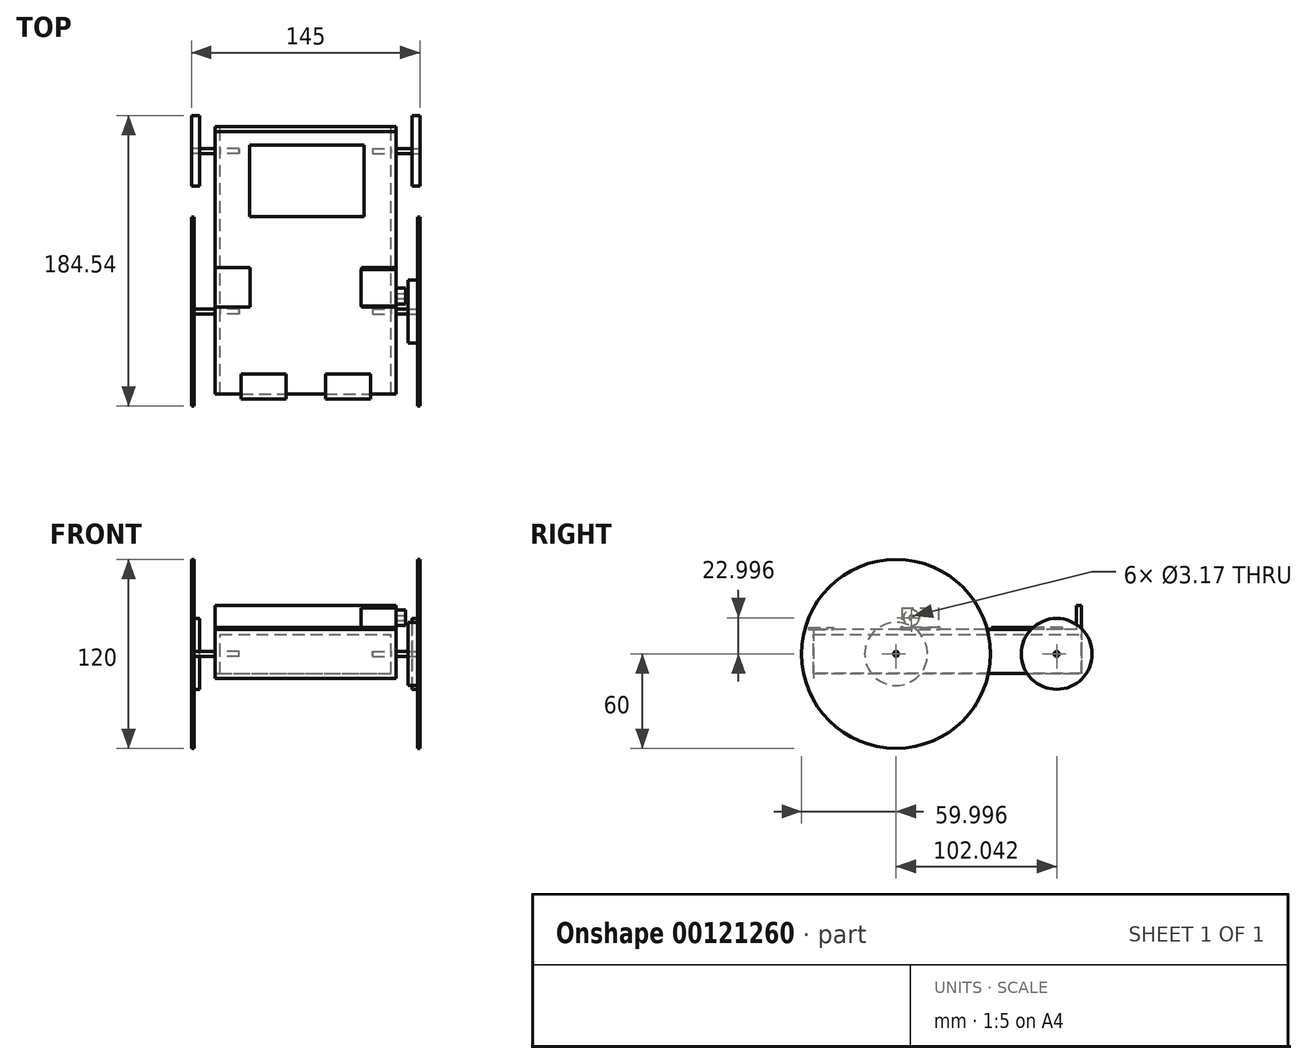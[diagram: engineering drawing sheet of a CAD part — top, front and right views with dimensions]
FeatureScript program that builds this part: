
annotation { "Feature Type Name" : "Feature", "Feature Type Description" : "" }
export const myFeature = defineFeature(function(context is Context, id is Id, definition is map)
    precondition{}
    {
        {
            var Q0;
            Q0=qCreatedBy(makeId("Top.planeOp"),FACE);
            var sketch = newSketch(context, id + "F0", { "sketchPlane" : qUnion([Q0])});
            skLineSegment(sketch, "E0.bottom", {"start": v(-104.64, 92.67) * mm, "end": v(10.36, 92.67) * mm});
            skLineSegment(sketch, "E0.top", {"start": v(-104.64, -77.33) * mm, "end": v(10.36, -77.33) * mm});
            skLineSegment(sketch, "E0.left", {"start": v(-104.64, 92.67) * mm, "end": v(-104.64, -77.33) * mm});
            skLineSegment(sketch, "E0.right", {"start": v(10.36, 92.67) * mm, "end": v(10.36, -77.33) * mm});
            skSolve(sketch);
        }
        {
            var Q0;
            Q0 = qSketchRegion(id + "F0", true);
            extrude(context, id + "F1", {"entities" : qUnion([Q0]), "depth" : 3.17 * mm});
        }
        {
            var Q0;
            Q0=makeQuery(id+"F1.opExtrude","CAP_FACE",FACE,{"disambiguationData":[OSD([sQuery(id+"F0.wireOp",EDGE,"E0.bottom"),sQuery(id+"F0.wireOp",EDGE,"E0.top"),sQuery(id+"F0.wireOp",EDGE,"E0.left"),sQuery(id+"F0.wireOp",EDGE,"E0.right")])],"isStart":true});
            var sketch = newSketch(context, id + "F2", { "sketchPlane" : qUnion([Q0])});
            skLineSegment(sketch, "E1.bottom", {"start": v(-104.64, 77.33) * mm, "end": v(-101.47, 77.33) * mm});
            skLineSegment(sketch, "E1.top", {"start": v(-104.64, -92.67) * mm, "end": v(-101.47, -92.67) * mm});
            skLineSegment(sketch, "E1.left", {"start": v(-104.64, 77.33) * mm, "end": v(-104.64, -92.67) * mm});
            skLineSegment(sketch, "E1.right", {"start": v(-101.47, 77.33) * mm, "end": v(-101.47, -92.67) * mm});
            skLineSegment(sketch, "E2.bottom", {"start": v(10.36, 77.33) * mm, "end": v(7.18, 77.33) * mm});
            skLineSegment(sketch, "E2.top", {"start": v(10.36, -92.67) * mm, "end": v(7.18, -92.67) * mm});
            skLineSegment(sketch, "E2.left", {"start": v(10.36, 77.33) * mm, "end": v(10.36, -92.67) * mm});
            skLineSegment(sketch, "E2.right", {"start": v(7.18, 77.33) * mm, "end": v(7.18, -92.67) * mm});
            skLineSegment(sketch, "E3.bottom", {"start": v(-68.47, 77.33) * mm, "end": v(-65.3, 77.33) * mm});
            skLineSegment(sketch, "E3.top", {"start": v(-68.47, -92.67) * mm, "end": v(-65.3, -92.67) * mm});
            skLineSegment(sketch, "E4.bottom", {"start": v(-29, 77.33) * mm, "end": v(-25.82, 77.33) * mm});
            skLineSegment(sketch, "E4.top", {"start": v(-29, -92.67) * mm, "end": v(-25.82, -92.67) * mm});
            skSolve(sketch);
        }
        {
            var Q0;
            Q0 = qSketchRegion(id + "F2", true);
            extrude(context, id + "F3", {"entities" : qUnion([Q0]), "operationType" : NewBodyOperationType.ADD, "depth" : 25 * mm});
        }
        {
            var Q0;
            Q0=makeQuery(id+"F3.opExtrude","CAP_FACE",FACE,{"disambiguationData":[OSD([sQuery(id+"F2.wireOp",EDGE,"E1.bottom"),sQuery(id+"F2.wireOp",EDGE,"E1.top"),sQuery(id+"F2.wireOp",EDGE,"E1.left"),sQuery(id+"F2.wireOp",EDGE,"E1.right")])],"isStart":false});
            var sketch = newSketch(context, id + "F4", { "sketchPlane" : qUnion([Q0])});
            skLineSegment(sketch, "E5.bottom", {"start": v(-104.64, 77.33) * mm, "end": v(10.36, 77.33) * mm});
            skLineSegment(sketch, "E5.top", {"start": v(-104.64, -92.67) * mm, "end": v(10.36, -92.67) * mm});
            skLineSegment(sketch, "E5.left", {"start": v(-104.64, 77.33) * mm, "end": v(-104.64, -92.67) * mm});
            skLineSegment(sketch, "E5.right", {"start": v(10.36, 77.33) * mm, "end": v(10.36, -92.67) * mm});
            skSolve(sketch);
        }
        {
            var Q0;
            Q0 = qSketchRegion(id + "F4", true);
            extrude(context, id + "F5", {"entities" : qUnion([Q0]), "operationType" : NewBodyOperationType.ADD, "depth" : 1 / 203.2 * mm});
        }
        {
            var Q0;
            Q0=makeQuery(id+"F5.boolean.opBoolean","MERGE",FACE,{"derivedFrom":[makeQuery(id+"F3.boolean.opBoolean","MERGE",FACE,{"derivedFrom":[makeQuery(id+"F1.opExtrude","SWEPT_FACE",FACE,{"disambiguationData":[OSD([sQuery(id+"F0.wireOp",EDGE,"E0.top")])]}),makeQuery(id+"F3.opExtrude","SWEPT_FACE",FACE,{"disambiguationData":[OSD([sQuery(id+"F2.wireOp",EDGE,"E1.bottom")])]}),makeQuery(id+"F3.opExtrude","SWEPT_FACE",FACE,{"disambiguationData":[OSD([sQuery(id+"F2.wireOp",EDGE,"E2.bottom")])]})]}),makeQuery(id+"F5.opExtrude","SWEPT_FACE",FACE,{"disambiguationData":[OSD([sQuery(id+"F4.wireOp",EDGE,"E5.bottom")])]})]});
            var sketch = newSketch(context, id + "F6", { "sketchPlane" : qUnion([Q0])});
            skLineSegment(sketch, "E6.bottom", {"start": v(-104.64, 3.18) * mm, "end": v(10.36, 3.18) * mm});
            skLineSegment(sketch, "E6.top", {"start": v(-104.64, -28.18) * mm, "end": v(10.36, -28.18) * mm});
            skLineSegment(sketch, "E6.left", {"start": v(-104.64, 3.18) * mm, "end": v(-104.64, -28.18) * mm});
            skLineSegment(sketch, "E6.right", {"start": v(10.36, 3.18) * mm, "end": v(10.36, -28.18) * mm});
            skSolve(sketch);
        }
        {
            var Q0;
            Q0 = qSketchRegion(id + "F6", true);
            extrude(context, id + "F7", {"entities" : qUnion([Q0]), "operationType" : NewBodyOperationType.ADD, "depth" : 1 / 203.2 * mm});
        }
        {
            var Q0;
            Q0=makeQuery(id+"F7.boolean.opBoolean","MERGE",FACE,{"derivedFrom":[makeQuery(id+"F1.opExtrude","CAP_FACE",FACE,{"disambiguationData":[OSD([sQuery(id+"F0.wireOp",EDGE,"E0.bottom"),sQuery(id+"F0.wireOp",EDGE,"E0.top"),sQuery(id+"F0.wireOp",EDGE,"E0.left"),sQuery(id+"F0.wireOp",EDGE,"E0.right")])],"isStart":false}),makeQuery(id+"F7.opExtrude","SWEPT_FACE",FACE,{"disambiguationData":[OSD([sQuery(id+"F6.wireOp",EDGE,"E6.bottom")])]})]});
            var sketch = newSketch(context, id + "F8", { "sketchPlane" : qUnion([Q0])});
            skLineSegment(sketch, "E7.bottom", {"start": v(-104.64, 92.67) * mm, "end": v(10.36, 92.67) * mm});
            skLineSegment(sketch, "E7.top", {"start": v(-104.64, 89.5) * mm, "end": v(10.36, 89.5) * mm});
            skLineSegment(sketch, "E7.left", {"start": v(-104.64, 92.67) * mm, "end": v(-104.64, 89.5) * mm});
            skLineSegment(sketch, "E7.right", {"start": v(10.36, 92.67) * mm, "end": v(10.36, 89.5) * mm});
            skSolve(sketch);
        }
        {
            var Q0;
            Q0 = qSketchRegion(id + "F8", true);
            extrude(context, id + "F9", {"entities" : qUnion([Q0]), "operationType" : NewBodyOperationType.ADD, "depth" : 15 * mm});
        }
        {
            var Q0;
            Q0=makeQuery(id+"F9.boolean.opBoolean","MERGE",FACE,{"derivedFrom":[makeQuery(id+"F7.boolean.opBoolean","MERGE",FACE,{"derivedFrom":[makeQuery(id+"F5.boolean.opBoolean","MERGE",FACE,{"derivedFrom":[makeQuery(id+"F3.boolean.opBoolean","MERGE",FACE,{"derivedFrom":[makeQuery(id+"F1.opExtrude","SWEPT_FACE",FACE,{"disambiguationData":[OSD([sQuery(id+"F0.wireOp",EDGE,"E0.right")])]}),makeQuery(id+"F3.opExtrude","SWEPT_FACE",FACE,{"disambiguationData":[OSD([sQuery(id+"F2.wireOp",EDGE,"E2.left")])]})]}),makeQuery(id+"F5.opExtrude","SWEPT_FACE",FACE,{"disambiguationData":[OSD([sQuery(id+"F4.wireOp",EDGE,"E5.right")])]})]}),makeQuery(id+"F7.opExtrude","SWEPT_FACE",FACE,{"disambiguationData":[OSD([sQuery(id+"F6.wireOp",EDGE,"E6.right")])]})]}),makeQuery(id+"F9.opExtrude","SWEPT_FACE",FACE,{"disambiguationData":[OSD([sQuery(id+"F8.wireOp",EDGE,"E7.right")])]})]});
            var sketch = newSketch(context, id + "F10", { "sketchPlane" : qUnion([Q0])});
            skCircle(sketch, "E8", {"center": v(-24.94, -12.5) * mm, "radius": 1.59 * mm});
            skPoint(sketch, "E8.centerSnap0", {"position": v(-80.5, -12.5) * mm});
            skCircle(sketch, "E9", {"center": v(77.1, -12.5) * mm, "radius": 1.59 * mm});
            skSolve(sketch);
        }
        {
            var Q0;
            Q0 = qSketchRegion(id + "F10", true);
            extrude(context, id + "F11", {"entities" : qUnion([Q0]), "operationType" : NewBodyOperationType.REMOVE, "endBound" : BoundingType.THROUGH_ALL, "oppositeDirection" : true, "depth" : 25 * mm});
        }
        {
            var Q0;
            Q0=makeQuery(id+"F9.boolean.opBoolean","MERGE",FACE,{"derivedFrom":[makeQuery(id+"F7.boolean.opBoolean","MERGE",FACE,{"derivedFrom":[makeQuery(id+"F5.boolean.opBoolean","MERGE",FACE,{"derivedFrom":[makeQuery(id+"F3.boolean.opBoolean","MERGE",FACE,{"derivedFrom":[makeQuery(id+"F1.opExtrude","SWEPT_FACE",FACE,{"disambiguationData":[OSD([sQuery(id+"F0.wireOp",EDGE,"E0.right")])]}),makeQuery(id+"F3.opExtrude","SWEPT_FACE",FACE,{"disambiguationData":[OSD([sQuery(id+"F2.wireOp",EDGE,"E2.left")])]})]}),makeQuery(id+"F5.opExtrude","SWEPT_FACE",FACE,{"disambiguationData":[OSD([sQuery(id+"F4.wireOp",EDGE,"E5.right")])]})]}),makeQuery(id+"F7.opExtrude","SWEPT_FACE",FACE,{"disambiguationData":[OSD([sQuery(id+"F6.wireOp",EDGE,"E6.right")])]})]}),makeQuery(id+"F9.opExtrude","SWEPT_FACE",FACE,{"disambiguationData":[OSD([sQuery(id+"F8.wireOp",EDGE,"E7.right")])]})]});
            var sketch = newSketch(context, id + "F12", { "sketchPlane" : qUnion([Q0])});
            skCircle(sketch, "E10", {"center": v(-24.94, -12.5) * mm, "radius": 1.59 * mm});
            skSolve(sketch);
        }
        {
            var Q0;
            Q0 = qSketchRegion(id + "F12", true);
            extrude(context, id + "F13", {"entities" : qUnion([Q0]), "oppositeDirection" : true, "depth" : 15 * mm});
        }
        {
            var Q0;
            Q0=makeQuery(id+"F13.opExtrude","CAP_FACE",FACE,{"disambiguationData":[OSD([sQuery(id+"F12.wireOp",EDGE,"E10")])],"isStart":true});
            var sketch = newSketch(context, id + "F14", { "sketchPlane" : qUnion([Q0])});
            skCircle(sketch, "E11", {"center": v(-24.94, -12.5) * mm, "radius": 1.59 * mm});
            skSolve(sketch);
        }
        {
            var Q0;
            Q0 = qSketchRegion(id + "F14", true);
            extrude(context, id + "F15", {"entities" : qUnion([Q0]), "operationType" : NewBodyOperationType.ADD, "depth" : 15 * mm});
        }
        {
            var Q0;
            Q0=makeQuery(id+"F9.boolean.opBoolean","MERGE",FACE,{"derivedFrom":[makeQuery(id+"F7.boolean.opBoolean","MERGE",FACE,{"derivedFrom":[makeQuery(id+"F5.boolean.opBoolean","MERGE",FACE,{"derivedFrom":[makeQuery(id+"F3.boolean.opBoolean","MERGE",FACE,{"derivedFrom":[makeQuery(id+"F1.opExtrude","SWEPT_FACE",FACE,{"disambiguationData":[OSD([sQuery(id+"F0.wireOp",EDGE,"E0.right")])]}),makeQuery(id+"F3.opExtrude","SWEPT_FACE",FACE,{"disambiguationData":[OSD([sQuery(id+"F2.wireOp",EDGE,"E2.left")])]})]}),makeQuery(id+"F5.opExtrude","SWEPT_FACE",FACE,{"disambiguationData":[OSD([sQuery(id+"F4.wireOp",EDGE,"E5.right")])]})]}),makeQuery(id+"F7.opExtrude","SWEPT_FACE",FACE,{"disambiguationData":[OSD([sQuery(id+"F6.wireOp",EDGE,"E6.right")])]})]}),makeQuery(id+"F9.opExtrude","SWEPT_FACE",FACE,{"disambiguationData":[OSD([sQuery(id+"F8.wireOp",EDGE,"E7.right")])]})]});
            var sketch = newSketch(context, id + "F16", { "sketchPlane" : qUnion([Q0])});
            skCircle(sketch, "E12", {"center": v(77.1, -12.5) * mm, "radius": 1.59 * mm});
            skSolve(sketch);
        }
        {
            var Q0;
            Q0 = qSketchRegion(id + "F16", true);
            extrude(context, id + "F17", {"entities" : qUnion([Q0]), "oppositeDirection" : true, "depth" : 15 * mm});
        }
        {
            var Q0;
            Q0=makeQuery(id+"F17.opExtrude","CAP_FACE",FACE,{"disambiguationData":[OSD([sQuery(id+"F16.wireOp",EDGE,"E12")])],"isStart":true});
            var sketch = newSketch(context, id + "F18", { "sketchPlane" : qUnion([Q0])});
            skCircle(sketch, "E13", {"center": v(77.1, -12.5) * mm, "radius": 1.59 * mm});
            skSolve(sketch);
        }
        {
            var Q0;
            Q0 = qSketchRegion(id + "F18", true);
            extrude(context, id + "F19", {"entities" : qUnion([Q0]), "operationType" : NewBodyOperationType.ADD, "depth" : 15 * mm});
        }
        {
            var Q0;
            Q0=makeQuery(id+"F9.boolean.opBoolean","MERGE",FACE,{"derivedFrom":[makeQuery(id+"F7.boolean.opBoolean","MERGE",FACE,{"derivedFrom":[makeQuery(id+"F5.boolean.opBoolean","MERGE",FACE,{"derivedFrom":[makeQuery(id+"F3.boolean.opBoolean","MERGE",FACE,{"derivedFrom":[makeQuery(id+"F1.opExtrude","SWEPT_FACE",FACE,{"disambiguationData":[OSD([sQuery(id+"F0.wireOp",EDGE,"E0.left")])]}),makeQuery(id+"F3.opExtrude","SWEPT_FACE",FACE,{"disambiguationData":[OSD([sQuery(id+"F2.wireOp",EDGE,"E1.left")])]})]}),makeQuery(id+"F5.opExtrude","SWEPT_FACE",FACE,{"disambiguationData":[OSD([sQuery(id+"F4.wireOp",EDGE,"E5.left")])]})]}),makeQuery(id+"F7.opExtrude","SWEPT_FACE",FACE,{"disambiguationData":[OSD([sQuery(id+"F6.wireOp",EDGE,"E6.left")])]})]}),makeQuery(id+"F9.opExtrude","SWEPT_FACE",FACE,{"disambiguationData":[OSD([sQuery(id+"F8.wireOp",EDGE,"E7.left")])]})]});
            var sketch = newSketch(context, id + "F20", { "sketchPlane" : qUnion([Q0])});
            skCircle(sketch, "E14", {"center": v(24.94, -12.5) * mm, "radius": 1.59 * mm});
            skSolve(sketch);
        }
        {
            var Q0;
            Q0 = qSketchRegion(id + "F20", true);
            extrude(context, id + "F21", {"entities" : qUnion([Q0]), "oppositeDirection" : true, "depth" : 15 * mm});
        }
        {
            var Q0;
            Q0=makeQuery(id+"F21.opExtrude","CAP_FACE",FACE,{"disambiguationData":[OSD([sQuery(id+"F20.wireOp",EDGE,"E14")])],"isStart":true});
            var sketch = newSketch(context, id + "F22", { "sketchPlane" : qUnion([Q0])});
            skCircle(sketch, "E15", {"center": v(24.94, -12.5) * mm, "radius": 1.59 * mm});
            skSolve(sketch);
        }
        {
            var Q0;
            Q0 = qSketchRegion(id + "F22", true);
            extrude(context, id + "F23", {"entities" : qUnion([Q0]), "operationType" : NewBodyOperationType.ADD, "depth" : 15 * mm});
        }
        {
            var Q0;
            Q0=makeQuery(id+"F9.boolean.opBoolean","MERGE",FACE,{"derivedFrom":[makeQuery(id+"F7.boolean.opBoolean","MERGE",FACE,{"derivedFrom":[makeQuery(id+"F5.boolean.opBoolean","MERGE",FACE,{"derivedFrom":[makeQuery(id+"F3.boolean.opBoolean","MERGE",FACE,{"derivedFrom":[makeQuery(id+"F1.opExtrude","SWEPT_FACE",FACE,{"disambiguationData":[OSD([sQuery(id+"F0.wireOp",EDGE,"E0.left")])]}),makeQuery(id+"F3.opExtrude","SWEPT_FACE",FACE,{"disambiguationData":[OSD([sQuery(id+"F2.wireOp",EDGE,"E1.left")])]})]}),makeQuery(id+"F5.opExtrude","SWEPT_FACE",FACE,{"disambiguationData":[OSD([sQuery(id+"F4.wireOp",EDGE,"E5.left")])]})]}),makeQuery(id+"F7.opExtrude","SWEPT_FACE",FACE,{"disambiguationData":[OSD([sQuery(id+"F6.wireOp",EDGE,"E6.left")])]})]}),makeQuery(id+"F9.opExtrude","SWEPT_FACE",FACE,{"disambiguationData":[OSD([sQuery(id+"F8.wireOp",EDGE,"E7.left")])]})]});
            var sketch = newSketch(context, id + "F24", { "sketchPlane" : qUnion([Q0])});
            skCircle(sketch, "E16", {"center": v(-77.1, -12.5) * mm, "radius": 1.59 * mm});
            skSolve(sketch);
        }
        {
            var Q0;
            Q0 = qSketchRegion(id + "F24", true);
            extrude(context, id + "F25", {"entities" : qUnion([Q0]), "oppositeDirection" : true, "depth" : 15 * mm});
        }
        {
            var Q0;
            Q0=makeQuery(id+"F25.opExtrude","CAP_FACE",FACE,{"disambiguationData":[OSD([sQuery(id+"F24.wireOp",EDGE,"E16")])],"isStart":true});
            var sketch = newSketch(context, id + "F26", { "sketchPlane" : qUnion([Q0])});
            skCircle(sketch, "E17", {"center": v(-77.1, -12.5) * mm, "radius": 1.59 * mm});
            skSolve(sketch);
        }
        {
            var Q0;
            Q0 = qSketchRegion(id + "F26", true);
            extrude(context, id + "F27", {"entities" : qUnion([Q0]), "operationType" : NewBodyOperationType.ADD, "depth" : 15 * mm});
        }
        {
            var Q0;
            Q0=makeQuery(id+"F23.opExtrude","CAP_FACE",FACE,{"disambiguationData":[OSD([sQuery(id+"F22.wireOp",EDGE,"E15")])],"isStart":false});
            var sketch = newSketch(context, id + "F28", { "sketchPlane" : qUnion([Q0])});
            skCircle(sketch, "E18", {"center": v(24.94, -12.5) * mm, "radius": 60 * mm});
            skCircle(sketch, "E19", {"center": v(24.94, -12.5) * mm, "radius": 1.59 * mm});
            skSolve(sketch);
        }
        {
            var Q0;
            Q0=makeQuery(id+"F28.imprint","IMPRINT",FACE,{"disambiguationData":[TD([[makeQuery(id+"F28.imprint","IMPRINT",EDGE,{"derivedFrom":sQuery(id+"F28.wireOp",EDGE,"E18")}),1.0]])]});
            extrude(context, id + "F29", {"entities" : qUnion([Q0]), "oppositeDirection" : true, "depth" : 1.5 * mm});
        }
        {
            var Q0;
            Q0=makeQuery(id+"F15.opExtrude","CAP_FACE",FACE,{"disambiguationData":[OSD([sQuery(id+"F14.wireOp",EDGE,"E11")])],"isStart":false});
            var sketch = newSketch(context, id + "F30", { "sketchPlane" : qUnion([Q0])});
            skCircle(sketch, "E20", {"center": v(-24.94, -12.5) * mm, "radius": 60 * mm});
            skCircle(sketch, "E21", {"center": v(-24.94, -12.5) * mm, "radius": 1.59 * mm});
            skSolve(sketch);
        }
        {
            var Q0;
            Q0 = qSketchRegion(id + "F30", true);
            extrude(context, id + "F31", {"entities" : qUnion([Q0]), "oppositeDirection" : true, "depth" : 1.5 * mm});
        }
        {
            var Q0;
            Q0=makeQuery(id+"F19.opExtrude","CAP_FACE",FACE,{"disambiguationData":[OSD([sQuery(id+"F18.wireOp",EDGE,"E13")])],"isStart":false});
            var sketch = newSketch(context, id + "F32", { "sketchPlane" : qUnion([Q0])});
            skCircle(sketch, "E22", {"center": v(77.1, -12.5) * mm, "radius": 22.5 * mm});
            skSolve(sketch);
        }
        {
            var Q0;
            Q0=makeQuery(id+"F32.imprint","IMPRINT",FACE,{"disambiguationData":[TD([[makeQuery(id+"F32.imprint","IMPRINT",EDGE,{"derivedFrom":sQuery(id+"F32.wireOp",EDGE,"E22")}),1.0]])]});
            extrude(context, id + "F33", {"entities" : qUnion([Q0]), "oppositeDirection" : true, "depth" : 5 * mm});
        }
        {
            var Q0;
            Q0=makeQuery(id+"F27.opExtrude","CAP_FACE",FACE,{"disambiguationData":[OSD([sQuery(id+"F26.wireOp",EDGE,"E17")])],"isStart":false});
            var sketch = newSketch(context, id + "F34", { "sketchPlane" : qUnion([Q0])});
            skCircle(sketch, "E23", {"center": v(-77.1, -12.5) * mm, "radius": 22.5 * mm});
            skCircle(sketch, "E24", {"center": v(-77.1, -12.5) * mm, "radius": 1.59 * mm});
            skSolve(sketch);
        }
        {
            var Q0;
            Q0 = qSketchRegion(id + "F34", true);
            extrude(context, id + "F35", {"entities" : qUnion([Q0]), "oppositeDirection" : true, "depth" : 5 * mm});
        }
        {
            var Q0;
            Q0=makeQuery(id+"F31.opExtrude","CAP_FACE",FACE,{"disambiguationData":[OSD([sQuery(id+"F30.wireOp",EDGE,"E20"),sQuery(id+"F30.wireOp",EDGE,"E21")])],"isStart":false});
            var sketch = newSketch(context, id + "F36", { "sketchPlane" : qUnion([Q0])});
            skCircle(sketch, "E25", {"center": v(24.94, -12.5) * mm, "radius": 20 * mm});
            skCircle(sketch, "E26", {"center": v(24.94, -12.5) * mm, "radius": 1.59 * mm});
            skSolve(sketch);
        }
        {
            var Q0;
            Q0 = qSketchRegion(id + "F36", true);
            extrude(context, id + "F37", {"entities" : qUnion([Q0]), "depth" : 6 * mm});
        }
        {
            var Q0;
            Q0=makeQuery(id+"F7.boolean.opBoolean","MERGE",FACE,{"derivedFrom":[makeQuery(id+"F1.opExtrude","CAP_FACE",FACE,{"disambiguationData":[OSD([sQuery(id+"F0.wireOp",EDGE,"E0.bottom"),sQuery(id+"F0.wireOp",EDGE,"E0.top"),sQuery(id+"F0.wireOp",EDGE,"E0.left"),sQuery(id+"F0.wireOp",EDGE,"E0.right")])],"isStart":false}),makeQuery(id+"F7.opExtrude","SWEPT_FACE",FACE,{"disambiguationData":[OSD([sQuery(id+"F6.wireOp",EDGE,"E6.bottom")])]})]});
            var sketch = newSketch(context, id + "F38", { "sketchPlane" : qUnion([Q0])});
            skLineSegment(sketch, "E27.bottom", {"start": v(10.36, -22.18) * mm, "end": v(-11.64, -22.18) * mm});
            skLineSegment(sketch, "E27.top", {"start": v(10.36, 2.82) * mm, "end": v(-11.64, 2.82) * mm});
            skLineSegment(sketch, "E27.left", {"start": v(10.36, -22.18) * mm, "end": v(10.36, 2.82) * mm});
            skLineSegment(sketch, "E27.right", {"start": v(-11.64, -22.18) * mm, "end": v(-11.64, 2.82) * mm});
            skLineSegment(sketch, "E28.bottom", {"start": v(-82.64, -22.18) * mm, "end": v(-104.64, -22.18) * mm});
            skLineSegment(sketch, "E28.top", {"start": v(-82.64, 2.82) * mm, "end": v(-104.64, 2.82) * mm});
            skLineSegment(sketch, "E28.left", {"start": v(-82.64, -22.18) * mm, "end": v(-82.64, 2.82) * mm});
            skLineSegment(sketch, "E28.right", {"start": v(-104.64, -22.18) * mm, "end": v(-104.64, 2.82) * mm});
            skSolve(sketch);
        }
        {
            var Q0;
            Q0 = qSketchRegion(id + "F38", true);
            extrude(context, id + "F39", {"entities" : qUnion([Q0]), "operationType" : NewBodyOperationType.ADD, "depth" : 1 * mm});
        }
        {
            var Q0;
            Q0=makeQuery(id+"F39.opExtrude","CAP_FACE",FACE,{"disambiguationData":[OSD([sQuery(id+"F38.wireOp",EDGE,"E27.bottom"),sQuery(id+"F38.wireOp",EDGE,"E27.top"),sQuery(id+"F38.wireOp",EDGE,"E27.left"),sQuery(id+"F38.wireOp",EDGE,"E27.right")])],"isStart":false});
            var sketch = newSketch(context, id + "F40", { "sketchPlane" : qUnion([Q0])});
            skLineSegment(sketch, "E29.bottom", {"start": v(-11.88, -21.35) * mm, "end": v(10.12, -21.35) * mm});
            skLineSegment(sketch, "E29.top", {"start": v(-11.88, 1.85) * mm, "end": v(10.12, 1.85) * mm});
            skLineSegment(sketch, "E29.left", {"start": v(-11.88, -21.35) * mm, "end": v(-11.88, 1.85) * mm});
            skLineSegment(sketch, "E29.right", {"start": v(10.12, -21.35) * mm, "end": v(10.12, 1.85) * mm});
            skSolve(sketch);
        }
        {
            var Q0;
            Q0 = qSketchRegion(id + "F40", true);
            extrude(context, id + "F41", {"entities" : qUnion([Q0]), "depth" : 12.5 * mm});
        }
        {
            var Q0;
            Q0=makeQuery(id+"F41.opExtrude","SWEPT_FACE",FACE,{"disambiguationData":[OSD([sQuery(id+"F40.wireOp",EDGE,"E29.right")])]});
            var sketch = newSketch(context, id + "F42", { "sketchPlane" : qUnion([Q0])});
            skCircle(sketch, "E30", {"center": v(-15.2, 10.5) * mm, "radius": 1.59 * mm});
            skSolve(sketch);
        }
        {
            var Q0;
            Q0 = qSketchRegion(id + "F42", true);
            extrude(context, id + "F43", {"entities" : qUnion([Q0]), "operationType" : NewBodyOperationType.ADD, "depth" : 6 * mm});
        }
        {
            var Q0;
            Q0=makeQuery(id+"F43.opExtrude","CAP_FACE",FACE,{"disambiguationData":[OSD([sQuery(id+"F42.wireOp",EDGE,"E30")])],"isStart":false});
            var sketch = newSketch(context, id + "F44", { "sketchPlane" : qUnion([Q0])});
            skCircle(sketch, "E31", {"center": v(-15.2, 10.5) * mm, "radius": 5 * mm});
            skCircle(sketch, "E32", {"center": v(-15.2, 10.5) * mm, "radius": 1.59 * mm});
            skSolve(sketch);
        }
        {
            var Q0;
            Q0 = qSketchRegion(id + "F44", true);
            extrude(context, id + "F45", {"entities" : qUnion([Q0]), "oppositeDirection" : true, "depth" : 6 * mm});
        }
        {
            var Q0;
            Q0=makeQuery(id+"F7.boolean.opBoolean","MERGE",FACE,{"derivedFrom":[makeQuery(id+"F1.opExtrude","CAP_FACE",FACE,{"disambiguationData":[OSD([sQuery(id+"F0.wireOp",EDGE,"E0.bottom"),sQuery(id+"F0.wireOp",EDGE,"E0.top"),sQuery(id+"F0.wireOp",EDGE,"E0.left"),sQuery(id+"F0.wireOp",EDGE,"E0.right")])],"isStart":false}),makeQuery(id+"F7.opExtrude","SWEPT_FACE",FACE,{"disambiguationData":[OSD([sQuery(id+"F6.wireOp",EDGE,"E6.bottom")])]})]});
            var sketch = newSketch(context, id + "F46", { "sketchPlane" : qUnion([Q0])});
            skLineSegment(sketch, "E33.bottom", {"start": v(-82.74, 80.69) * mm, "end": v(-10, 80.69) * mm});
            skLineSegment(sketch, "E33.top", {"start": v(-82.74, 35.5) * mm, "end": v(-10, 35.5) * mm});
            skLineSegment(sketch, "E33.left", {"start": v(-82.74, 80.69) * mm, "end": v(-82.74, 35.5) * mm});
            skLineSegment(sketch, "E33.right", {"start": v(-10, 80.69) * mm, "end": v(-10, 35.5) * mm});
            skSolve(sketch);
        }
        {
            var Q0;
            Q0 = qSketchRegion(id + "F46", true);
            extrude(context, id + "F47", {"entities" : qUnion([Q0]), "operationType" : NewBodyOperationType.ADD, "depth" : 1 * mm});
        }
        {
            var Q0;
            Q0=makeQuery(id+"F7.boolean.opBoolean","MERGE",FACE,{"derivedFrom":[makeQuery(id+"F1.opExtrude","CAP_FACE",FACE,{"disambiguationData":[OSD([sQuery(id+"F0.wireOp",EDGE,"E0.bottom"),sQuery(id+"F0.wireOp",EDGE,"E0.top"),sQuery(id+"F0.wireOp",EDGE,"E0.left"),sQuery(id+"F0.wireOp",EDGE,"E0.right")])],"isStart":false}),makeQuery(id+"F7.opExtrude","SWEPT_FACE",FACE,{"disambiguationData":[OSD([sQuery(id+"F6.wireOp",EDGE,"E6.bottom")])]})]});
            var sketch = newSketch(context, id + "F48", { "sketchPlane" : qUnion([Q0])});
            skLineSegment(sketch, "E34.bottom", {"start": v(-88.26, -80.5) * mm, "end": v(-59.68, -80.5) * mm});
            skLineSegment(sketch, "E34.top", {"start": v(-88.26, -64.63) * mm, "end": v(-59.68, -64.63) * mm});
            skLineSegment(sketch, "E34.left", {"start": v(-88.26, -80.5) * mm, "end": v(-88.26, -64.63) * mm});
            skLineSegment(sketch, "E34.right", {"start": v(-59.68, -80.5) * mm, "end": v(-59.68, -64.63) * mm});
            skLineSegment(sketch, "E35.bottom", {"start": v(-34.68, -80.5) * mm, "end": v(-6.1, -80.5) * mm});
            skLineSegment(sketch, "E35.top", {"start": v(-34.68, -64.63) * mm, "end": v(-6.1, -64.63) * mm});
            skLineSegment(sketch, "E35.left", {"start": v(-34.68, -80.5) * mm, "end": v(-34.68, -64.63) * mm});
            skLineSegment(sketch, "E35.right", {"start": v(-6.1, -80.5) * mm, "end": v(-6.1, -64.63) * mm});
            skSolve(sketch);
        }
        {
            var Q0;
            Q0 = qSketchRegion(id + "F48", true);
            extrude(context, id + "F49", {"entities" : qUnion([Q0]), "operationType" : NewBodyOperationType.ADD, "depth" : 1 * mm});
        }
    });
